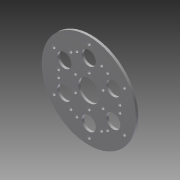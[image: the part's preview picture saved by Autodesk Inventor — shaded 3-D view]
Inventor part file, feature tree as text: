
AUTODESK INVENTOR PART (.ipt)
format: ipt  version: 2014 (Build 180170000, 170)  size: 162,304 bytes
history: native  units: in
note: dims shown in document units (in); Inventor stores cm internally (conversion verified against a paired STEP export)
features: sheet_metal_op x4, sketch x2, other x2
ambient origin geometry x8: Origin, YZ Plane, XZ Plane, XY Plane, X Axis, Y Axis, Z Axis, Center Point
bodies: Solid1 (feature_tree)
feature tree (8):
  sheet_metal_op  "Face1"
  sheet_metal_op  "Flange1"
  sketch  "Sketch1"  dims[d1=2.3622in d2=5.0in d3=1.125in d4=0.503in d5=1.625in d6=1.31in d7=0.1875in d8=0.1875in d9=0.1875in d10=0.1875in d11=360.0deg]
  other  "Plate1"
  sketch  "Sketch2"  dims[d12=0.125in d13=0.125in d14=0.0625in d15=0.25in d16=0.125in d17=1.0in d18=90.0deg d19=0.125in d20=0.5in d21=0.125in d22=0.125in]
  other  "Plate2"
  sheet_metal_op  "Bend1"
  sheet_metal_op  "Corner1"
